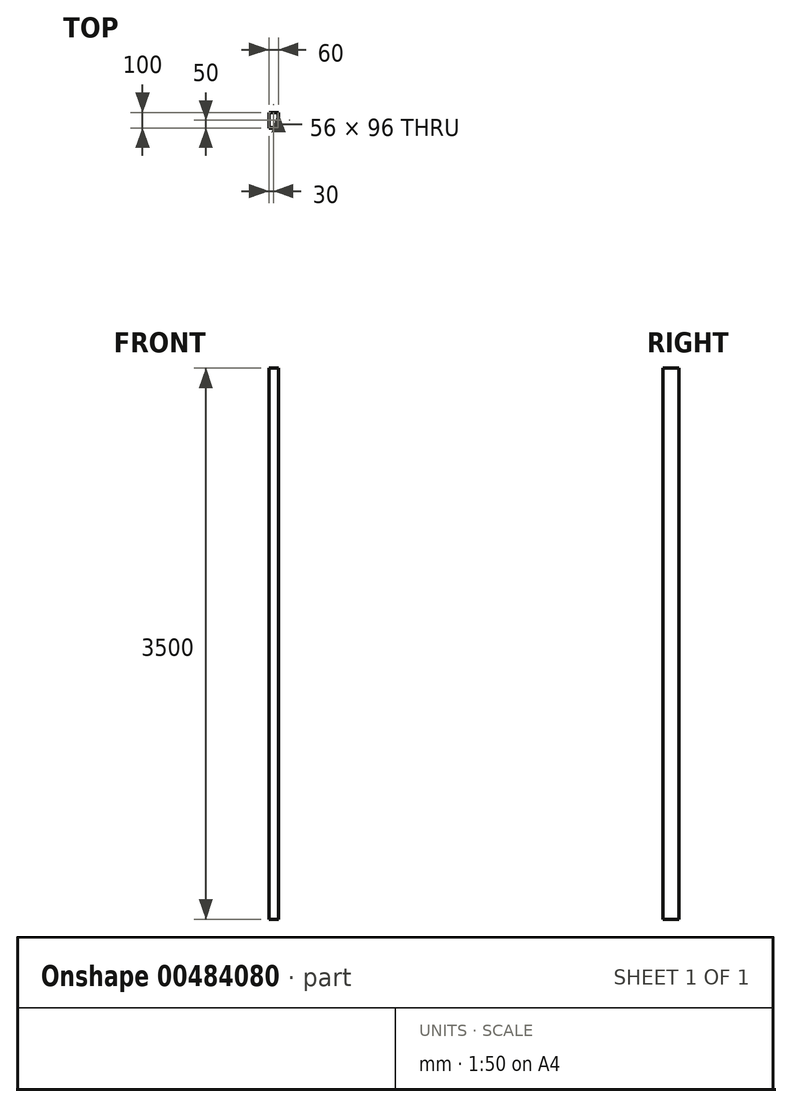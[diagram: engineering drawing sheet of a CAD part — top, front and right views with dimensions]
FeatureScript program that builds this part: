
annotation { "Feature Type Name" : "Feature", "Feature Type Description" : "" }
export const myFeature = defineFeature(function(context is Context, id is Id, definition is map)
    precondition{}
    {
        {
            var Q0;
            Q0=qCreatedBy(makeId("Top.planeOp"),FACE);
            var sketch = newSketch(context, id + "F0", { "sketchPlane" : qUnion([Q0])});
            skLineSegment(sketch, "E0.bottom", {"start": v(0, 0) * mm, "end": v(-60, 0) * mm});
            skLineSegment(sketch, "E0.top", {"start": v(0, -100) * mm, "end": v(-60, -100) * mm});
            skLineSegment(sketch, "E0.left", {"start": v(0, 0) * mm, "end": v(0, -100) * mm});
            skLineSegment(sketch, "E0.right", {"start": v(-60, 0) * mm, "end": v(-60, -100) * mm});
            skLineSegment(sketch, "E1.bottom", {"start": v(-58, -2) * mm, "end": v(-2, -2) * mm});
            skLineSegment(sketch, "E1.top", {"start": v(-58, -98) * mm, "end": v(-2, -98) * mm});
            skLineSegment(sketch, "E1.left", {"start": v(-58, -2) * mm, "end": v(-58, -98) * mm});
            skLineSegment(sketch, "E1.right", {"start": v(-2, -2) * mm, "end": v(-2, -98) * mm});
            skSolve(sketch);
        }
        {
            var Q0;
            Q0 = qSketchRegion(id + "F0", true);
            extrude(context, id + "F1", {"entities" : qUnion([Q0]), "depth" : 3500 * mm, "offsetDistance" : 25 * mm});
        }
    });
